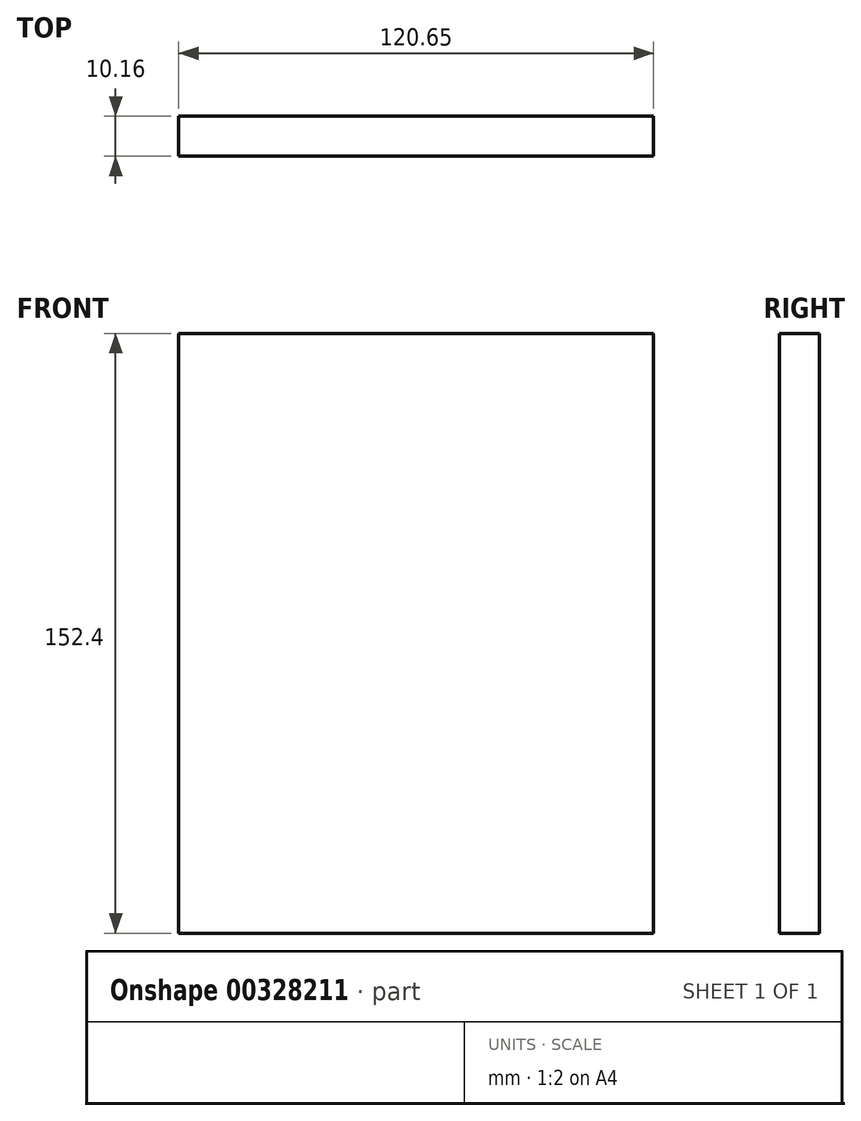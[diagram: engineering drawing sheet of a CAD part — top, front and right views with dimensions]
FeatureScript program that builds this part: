
annotation { "Feature Type Name" : "Feature", "Feature Type Description" : "" }
export const myFeature = defineFeature(function(context is Context, id is Id, definition is map)
    precondition{}
    {
        {
            var Q0;
            Q0=qCreatedBy(makeId("Front.planeOp"),FACE);
            var sketch = newSketch(context, id + "F0", { "sketchPlane" : qUnion([Q0])});
            skLineSegment(sketch, "E0", {"start": v(-73.64, 84.02) * mm, "end": v(47.01, 84.02) * mm});
            skLineSegment(sketch, "E1", {"start": v(47.01, 84.02) * mm, "end": v(47.01, -68.38) * mm});
            skLineSegment(sketch, "E2", {"start": v(47.01, -68.38) * mm, "end": v(-73.64, -68.38) * mm});
            skLineSegment(sketch, "E3", {"start": v(-73.64, -68.38) * mm, "end": v(-73.64, 84.02) * mm});
            skSolve(sketch);
        }
        {
            var Q0;
            Q0=makeQuery(id+"F0.imprint","IMPRINT",FACE,{"disambiguationData":[TD([[makeQuery(id+"F0.imprint","IMPRINT",EDGE,{"derivedFrom":sQuery(id+"F0.wireOp",EDGE,"E0")}),-1.0]])]});
            extrude(context, id + "F1", {"entities" : qUnion([Q0]), "depth" : 10.16 * mm});
        }
    });
